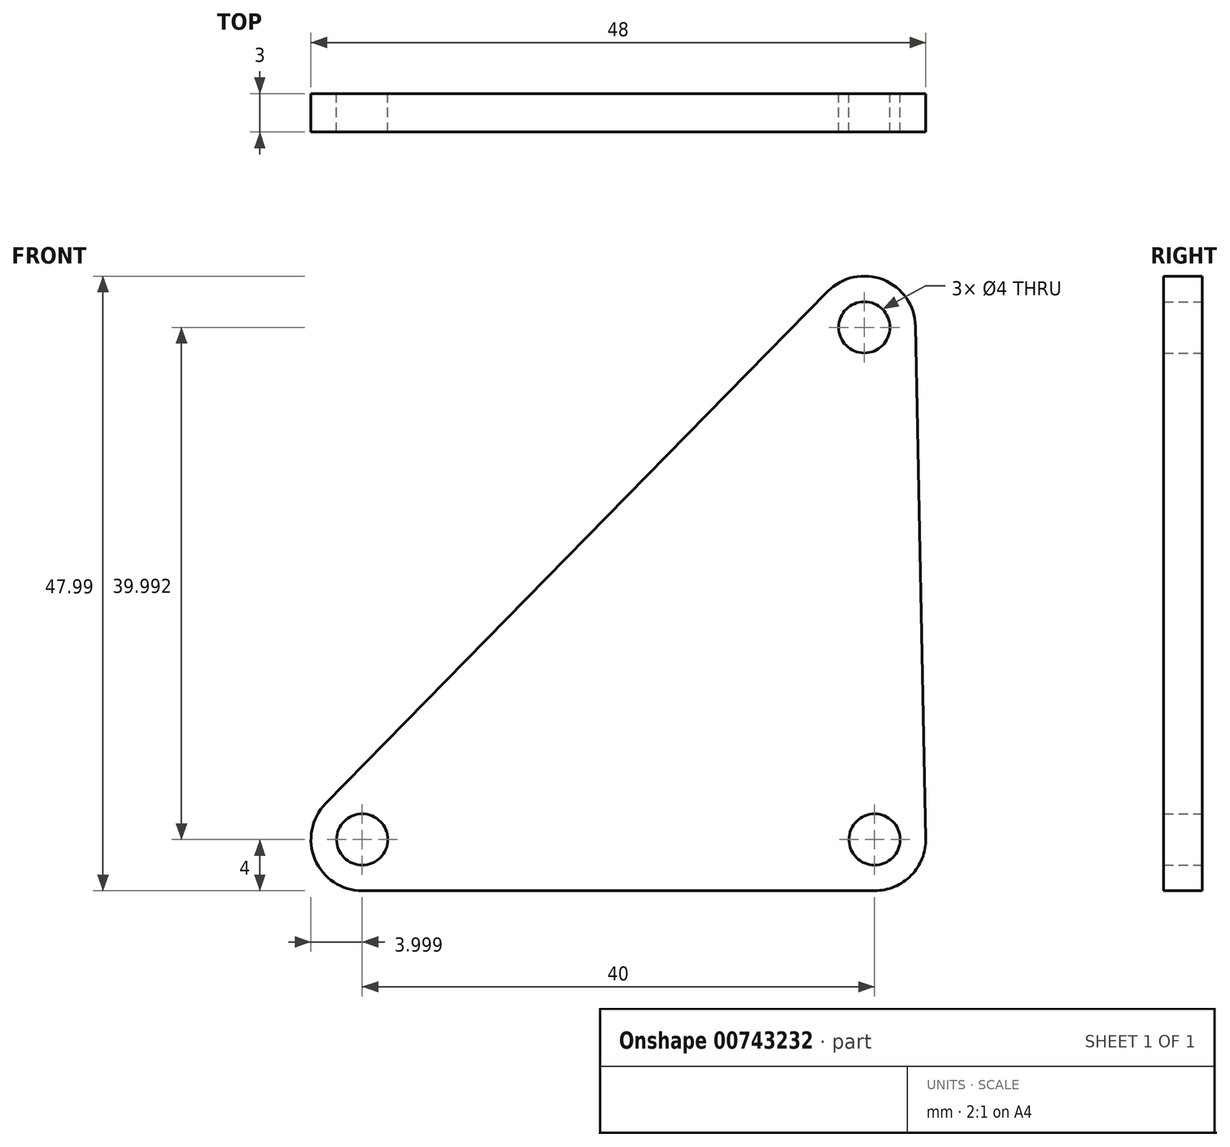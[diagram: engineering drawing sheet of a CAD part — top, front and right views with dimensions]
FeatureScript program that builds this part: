
annotation { "Feature Type Name" : "Feature", "Feature Type Description" : "" }
export const myFeature = defineFeature(function(context is Context, id is Id, definition is map)
    precondition{}
    {
        {
            var Q0;
            Q0=qCreatedBy(makeId("Front.planeOp"),FACE);
            var sketch = newSketch(context, id + "F0", { "sketchPlane" : qUnion([Q0])});
            skLineSegment(sketch, "E0", {"start": v(-0.08, 4.08) * mm, "end": v(-0.88, 44.07) * mm});
            skLineSegment(sketch, "E1", {"start": v(-7.74, 46.8) * mm, "end": v(-46.94, 6.8) * mm});
            skLineSegment(sketch, "E2", {"start": v(-44.08, 0) * mm, "end": v(-4.08, 0) * mm});
            skPoint(sketch, "E3.visualSharp", {"position": v(-1.07, 53.6) * mm});
            skArc(sketch, "E3.filletArc", {"start": v(-0.88, 44.07) * mm, "mid": v(-3.4, 47.71) * mm, "end": v(-7.74, 46.8) * mm});
            skPoint(sketch, "E4.visualSharp", {"position": v(-53.6, 0) * mm});
            skArc(sketch, "E4.filletArc", {"start": v(-46.94, 6.8) * mm, "mid": v(-47.77, 2.45) * mm, "end": v(-44.08, 0) * mm});
            skPoint(sketch, "E5.visualSharp", {"position": v(0, 0) * mm});
            skArc(sketch, "E5.filletArc", {"start": v(-4.08, 0) * mm, "mid": v(-1.22, 1.2) * mm, "end": v(-0.08, 4.08) * mm});
            skCircle(sketch, "E6", {"center": v(-44.08, 4) * mm, "radius": 2 * mm});
            skCircle(sketch, "E7", {"center": v(-4.08, 4) * mm, "radius": 2 * mm});
            skCircle(sketch, "E8", {"center": v(-4.88, 44) * mm, "radius": 2 * mm});
            skSolve(sketch);
        }
        {
            var Q0;
            Q0=qSketchRegion(id+"F0",true);
            extrude(context, id + "F1", {"entities" : qUnion([Q0]), "depth" : 3 * mm, "offsetDistance" : 25 * mm});
        }
    });
